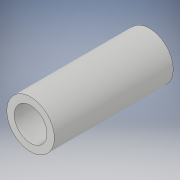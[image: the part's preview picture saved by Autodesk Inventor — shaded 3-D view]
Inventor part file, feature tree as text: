
AUTODESK INVENTOR PART (.ipt)
format: ipt  version: 2017 (Build 210142000, 142)  size: 94,720 bytes
history: native  units: in
note: dims shown in document units (in); Inventor stores cm internally (conversion verified against a paired STEP export)
features: extrude x1, sketch x1
ambient origin geometry x8: Origin, YZ Plane, XZ Plane, XY Plane, X Axis, Y Axis, Z Axis, Center Point
bodies: Solid1 (feature_tree)
feature tree (2):
  extrude  "Extrusion1"  Depth=0.5in
  sketch  "Sketch1"  dims[d0=0.138in d1=0.2in d2=0.5in d3=0.0in]
